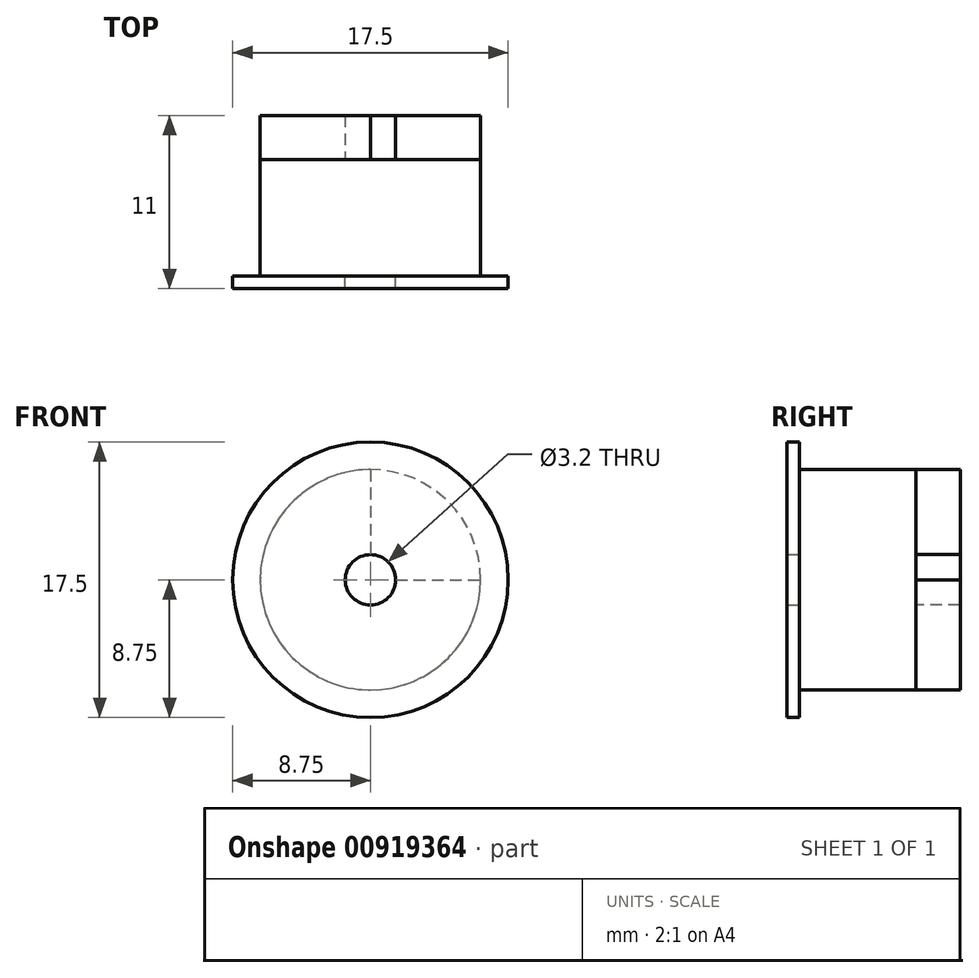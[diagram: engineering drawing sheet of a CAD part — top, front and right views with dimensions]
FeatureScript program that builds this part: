
annotation { "Feature Type Name" : "Feature", "Feature Type Description" : "" }
export const myFeature = defineFeature(function(context is Context, id is Id, definition is map)
    precondition{}
    {
        {
            var Q0;
            Q0=qCreatedBy(makeId("Front.planeOp"),FACE);
            var sketch = newSketch(context, id + "F0", { "sketchPlane" : qUnion([Q0])});
            skCircle(sketch, "E0", {"center": v(0, 0) * mm, "radius": 7 * mm});
            skSolve(sketch);
        }
        {
            var Q0;
            Q0=makeQuery(id+"F0.imprint","IMPRINT",FACE,{"disambiguationData":[TD([[makeQuery(id+"F0.imprint","IMPRINT",EDGE,{"derivedFrom":sQuery(id+"F0.wireOp",EDGE,"E0")}),1.0]])]});
            extrude(context, id + "F1", {"entities" : qUnion([Q0]), "depth" : 7.4 * mm, "offsetDistance" : 25 * mm});
        }
        {
            var Q0;
            Q0=makeQuery(id+"F1.opExtrude","CAP_FACE",FACE,{"disambiguationData":[OSD([sQuery(id+"F0.wireOp",EDGE,"E0")])],"isStart":false});
            var sketch = newSketch(context, id + "F2", { "sketchPlane" : qUnion([Q0])});
            skCircle(sketch, "E1", {"center": v(0, 0) * mm, "radius": 8.75 * mm});
            skCircle(sketch, "E2", {"center": v(0, 0) * mm, "radius": 1.6 * mm});
            skSolve(sketch);
        }
        {
            var Q0;
            Q0=makeQuery(id+"F2.imprint","IMPRINT",FACE,{"disambiguationData":[TD([[makeQuery(id+"F2.imprint","IMPRINT",EDGE,{"derivedFrom":sQuery(id+"F2.wireOp",EDGE,"E2")}),-1.0]])]});
            var Q1;
            Q1=makeQuery(id+"F2.imprint","IMPRINT",FACE,{"disambiguationData":[TD([[makeQuery(id+"F2.imprint","IMPRINT",EDGE,{"derivedFrom":sQuery(id+"F2.wireOp",EDGE,"E1")}),1.0]])]});
            extrude(context, id + "F3", {"entities" : qUnion([Q0, Q1]), "depth" : 0.8 * mm, "offsetDistance" : 25 * mm});
        }
        {
            var Q0;
            Q0=makeQuery(id+"F1.opExtrude","CAP_FACE",FACE,{"disambiguationData":[OSD([sQuery(id+"F0.wireOp",EDGE,"E0")])],"isStart":true});
            var sketch = newSketch(context, id + "F4", { "sketchPlane" : qUnion([Q0])});
            skArc(sketch, "E3", {"start": v(0, 7) * mm, "mid": v(4.95, -4.95) * mm, "end": v(-7, 0) * mm});
            skArc(sketch, "E4", {"start": v(0, 1.6) * mm, "mid": v(1.13, -1.13) * mm, "end": v(-1.6, 0) * mm});
            skLineSegment(sketch, "E5", {"start": v(0, 7) * mm, "end": v(0, 1.6) * mm});
            skLineSegment(sketch, "E6", {"start": v(-1.6, 0) * mm, "end": v(-7, 0) * mm});
            skSolve(sketch);
        }
        {
            var Q0;
            Q0 = qSketchRegion(id + "F4", true);
            extrude(context, id + "F5", {"entities" : qUnion([Q0]), "depth" : 2.8 * mm, "offsetDistance" : 25 * mm});
        }
    });
